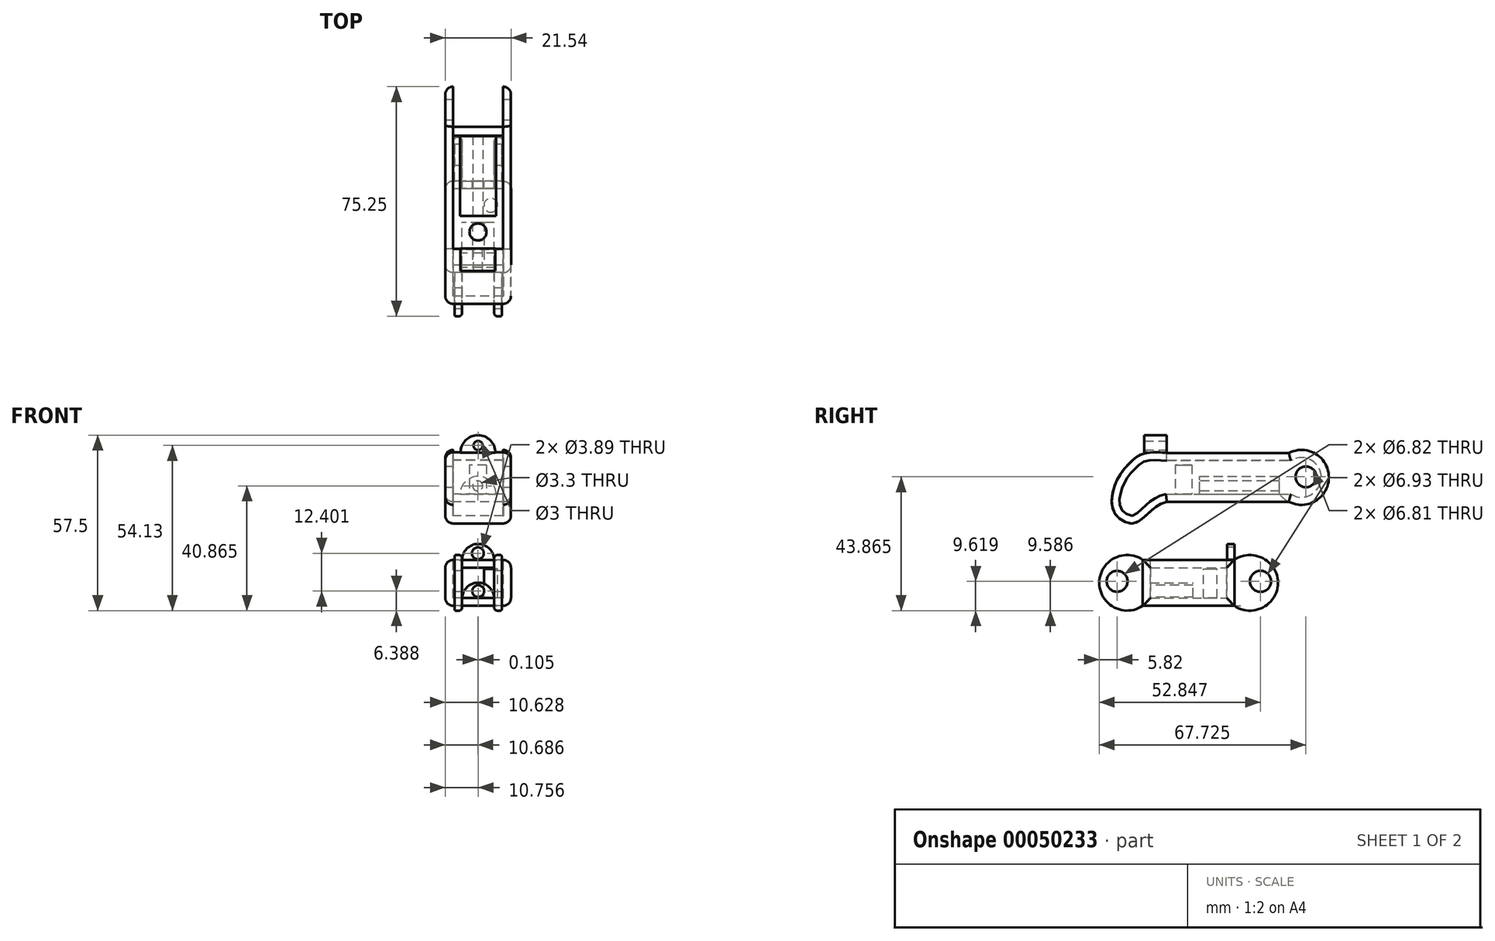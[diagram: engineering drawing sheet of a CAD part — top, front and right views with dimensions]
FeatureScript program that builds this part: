
annotation { "Feature Type Name" : "Feature", "Feature Type Description" : "" }
export const myFeature = defineFeature(function(context is Context, id is Id, definition is map)
    precondition{}
    {
        {
            var Q0;
            Q0=qCreatedBy(makeId("Right.planeOp"),FACE);
            var sketch = newSketch(context, id + "F0", { "sketchPlane" : qUnion([Q0])});
            skLineSegment(sketch, "E0.bottom", {"start": v(-17.03, 8) * mm, "end": v(22.97, 8) * mm});
            skLineSegment(sketch, "E0.top", {"start": v(-17.03, -8) * mm, "end": v(22.97, -8) * mm});
            skLineSegment(sketch, "E0.right", {"start": v(22.97, 8) * mm, "end": v(22.97, -8) * mm});
            skFitSpline(sketch, "E1", {"points": [v(-17.03, 8) * mm, v(-23.95, 8) * mm, v(-29.12, 4.72) * mm, v(-32.9, 0) * mm, v(-35.08, -8.22) * mm, v(-32.93, -13.14) * mm, v(-27.16, -14.86) * mm, v(-17.03, -8) * mm], "startDerivative": vector(-10.66, 0) * mm, "endDerivative": vector(74.6, 17.35) * mm});
            skLineSegment(sketch, "E2", {"start": v(-17.03, 8) * mm, "end": v(-17.03, -8) * mm});
            skArc(sketch, "E3", {"start": v(22.97, -8) * mm, "mid": v(36.1, 0) * mm, "end": v(22.97, 8) * mm});
            skLineSegment(sketch, "E4", {"start": v(-35.08, 39.3) * mm, "end": v(22.97, 39.3) * mm, "construction": true});
            skSolve(sketch);
        }
        {
            var Q0;
            Q0 = qSketchRegion(id + "F0", true);
            extrude(context, id + "F1", {"entities" : qUnion([Q0]), "depth" : 21.53 * mm});
        }
        {
            var Q0;
            Q0=makeQuery(id+"F1.opExtrude","CAP_EDGE",EDGE,{"disambiguationData":[OSD([sQuery(id+"F0.wireOp",EDGE,"E1")])],"isStart":false});
            var Q1;
            Q1=makeQuery(id+"F1.opExtrude","CAP_EDGE",EDGE,{"disambiguationData":[OSD([sQuery(id+"F0.wireOp",EDGE,"E0.bottom")])],"isStart":false});
            var Q2;
            Q2=makeQuery(id+"F1.opExtrude","CAP_EDGE",EDGE,{"disambiguationData":[OSD([sQuery(id+"F0.wireOp",EDGE,"E0.top")])],"isStart":false});
            var Q3;
            Q3=makeQuery(id+"F1.opExtrude","CAP_EDGE",EDGE,{"disambiguationData":[OSD([sQuery(id+"F0.wireOp",EDGE,"E0.right")])],"isStart":false});
            var Q4;
            Q4=makeQuery(id+"F1.opExtrude","CAP_EDGE",EDGE,{"disambiguationData":[OSD([sQuery(id+"F0.wireOp",EDGE,"ce066866-ab93-4ea4-af78-5b55cf1db8a8")])],"isStart":false});
            var Q5;
            Q5=makeQuery(id+"F1.opExtrude","CAP_EDGE",EDGE,{"disambiguationData":[OSD([sQuery(id+"F0.wireOp",EDGE,"E3")])],"isStart":false});
            fillet(context, id + "F2", {"entities" : qUnion([Q0, Q1, Q2, Q3, Q4, Q5]), "radius" : 2.54 * mm, "tangentPropagation" : true, "allowEdgeOverflow" : false});
        }
        {
            var Q0;
            Q0=makeQuery(id+"F1.opExtrude","CAP_EDGE",EDGE,{"disambiguationData":[OSD([sQuery(id+"F0.wireOp",EDGE,"E0.bottom")])],"isStart":true});
            var Q1;
            Q1=makeQuery(id+"F1.opExtrude","CAP_EDGE",EDGE,{"disambiguationData":[OSD([sQuery(id+"F0.wireOp",EDGE,"E1")])],"isStart":true});
            var Q2;
            Q2=makeQuery(id+"F1.opExtrude","CAP_FACE",FACE,{"disambiguationData":[OSD([sQuery(id+"F0.wireOp",EDGE,"E0.bottom"),sQuery(id+"F0.wireOp",EDGE,"E0.top"),sQuery(id+"F0.wireOp",EDGE,"E0.right"),sQuery(id+"F0.wireOp",EDGE,"E1")])],"isStart":true});
            var Q3;
            Q3=makeQuery(id+"F1.opExtrude","CAP_EDGE",EDGE,{"disambiguationData":[OSD([sQuery(id+"F0.wireOp",EDGE,"E0.top")])],"isStart":true});
            var Q4;
            Q4=makeQuery(id+"F1.opExtrude","CAP_EDGE",EDGE,{"disambiguationData":[OSD([sQuery(id+"F0.wireOp",EDGE,"E0.right")])],"isStart":true});
            fillet(context, id + "F3", {"entities" : qUnion([Q0, Q1, Q2, Q3, Q4]), "radius" : 2.54 * mm, "tangentPropagation" : true, "allowEdgeOverflow" : false});
        }
        {
            var Q0;
            Q0=makeQuery(id+"F1.opExtrude","SWEPT_FACE",FACE,{"disambiguationData":[OSD([sQuery(id+"F0.wireOp",EDGE,"E0.bottom")])]});
            var Q1;
            Q1=makeQuery(id+"F1.opExtrude","SWEPT_FACE",FACE,{"disambiguationData":[OSD([sQuery(id+"F0.wireOp",EDGE,"E3")])]});
            shell(context, id + "F4", {"entities" : qUnion([Q0, Q1]), "thickness" : 2.5 * mm});
        }
        {
            var Q0;
            Q0=qCreatedBy(makeId("Right.planeOp"),FACE);
            var sketch = newSketch(context, id + "F5", { "sketchPlane" : qUnion([Q0])});
            skCircle(sketch, "E5", {"center": v(28.57, 0.19) * mm, "radius": 3.4 * mm});
            skSolve(sketch);
        }
        {
            var Q0;
            Q0 = qSketchRegion(id + "F5", true);
            extrude(context, id + "F6", {"entities" : qUnion([Q0]), "operationType" : NewBodyOperationType.REMOVE, "oppositeDirection" : true, "depth" : 25 * mm, "hasSecondDirection" : true, "secondDirectionOppositeDirection" : false, "secondDirectionDepth" : 25 * mm});
        }
        {
            var Q0;
            Q0=qCreatedBy(makeId("Front.planeOp"),FACE);
            var sketch = newSketch(context, id + "F7", { "sketchPlane" : qUnion([Q0])});
            skLineSegment(sketch, "E6", {"start": v(2.57, -5.6) * mm, "end": v(18.95, -5.6) * mm});
            skArc(sketch, "E7", {"start": v(16.68, -5.6) * mm, "mid": v(10.76, 0.32) * mm, "end": v(4.84, -5.6) * mm});
            skSolve(sketch);
        }
        {
            var Q0;
            Q0 = qSketchRegion(id + "F7", true);
            var Q1;
            Q1=makeQuery(id+"F1.opExtrude","SWEPT_BODY",BODY,{"disambiguationData":[OSD([sQuery(id+"F0.wireOp",EDGE,"E0.bottom"),sQuery(id+"F0.wireOp",EDGE,"E0.top"),sQuery(id+"F0.wireOp",EDGE,"E1"),sQuery(id+"F0.wireOp",EDGE,"ce066866-ab93-4ea4-af78-5b55cf1db8a8")])]});
            extrude(context, id + "F8", {"entities" : qUnion([Q0]), "operationType" : NewBodyOperationType.ADD, "endBoundEntityBody" : qUnion([Q1]), "depth" : 6.26 * mm, "hasSecondDirection" : true, "secondDirectionOppositeDirection" : true, "secondDirectionDepth" : 19.94 * mm});
        }
        {
            var Q0;
            Q0=qCreatedBy(makeId("Front.planeOp"),FACE);
            var sketch = newSketch(context, id + "F9", { "sketchPlane" : qUnion([Q0])});
            skCircle(sketch, "E8", {"center": v(10.63, -2.81) * mm, "radius": 1.65 * mm});
            skSolve(sketch);
        }
        {
            var Q0;
            Q0 = qSketchRegion(id + "F9", true);
            extrude(context, id + "F10", {"entities" : qUnion([Q0]), "operationType" : NewBodyOperationType.REMOVE, "oppositeDirection" : true, "depth" : 23.72 * mm, "hasSecondDirection" : true, "secondDirectionOppositeDirection" : false, "secondDirectionDepth" : 7.27 * mm});
        }
        {
            var Q0;
            Q0=qCreatedBy(makeId("Top.planeOp"),FACE);
            var sketch = newSketch(context, id + "F11", { "sketchPlane" : qUnion([Q0])});
            skCircle(sketch, "E9", {"center": v(10.72, -11.53) * mm, "radius": 2.78 * mm});
            skSolve(sketch);
        }
        {
            var Q0;
            Q0=makeQuery(id+"F11.imprint","IMPRINT",FACE,{"disambiguationData":[TD([[makeQuery(id+"F11.imprint","IMPRINT",EDGE,{"derivedFrom":sQuery(id+"F11.wireOp",EDGE,"E9")}),1.0]])]});
            extrude(context, id + "F12", {"entities" : qUnion([Q0]), "operationType" : NewBodyOperationType.ADD, "depth" : 4.07 * mm, "hasSecondDirection" : true, "secondDirectionOppositeDirection" : true, "secondDirectionDepth" : 5.54 * mm});
        }
        {
            var Q0;
            Q0=qCreatedBy(makeId("Front.planeOp"),FACE);
            var sketch = newSketch(context, id + "F13", { "sketchPlane" : qUnion([Q0])});
            skLineSegment(sketch, "E10", {"start": v(1.36, 8.11) * mm, "end": v(20.04, 8.11) * mm});
            skPoint(sketch, "E11", {"position": v(10.7, 8.11) * mm});
            skArc(sketch, "E12", {"start": v(16.4, 8.11) * mm, "mid": v(10.7, 13.82) * mm, "end": v(5, 8.11) * mm});
            skSolve(sketch);
        }
        {
            var Q0;
            {var subQ0=sQuery(id+"F13.wireOp",EDGE,"E12");Q0=makeQuery(id+"F13.imprint","IMPRINT",FACE,{"disambiguationData":[TD([[makeQuery(id+"F13.imprint","IMPRINT",EDGE,{"derivedFrom":subQ0}),1.0]])]});}
            extrude(context, id + "F14", {"entities" : qUnion([Q0]), "operationType" : NewBodyOperationType.ADD, "depth" : 24.37 * mm, "hasSecondDirection" : true, "secondDirectionOppositeDirection" : false, "secondDirectionDepth" : 17 * mm});
        }
        {
            var Q0;
            Q0=qCreatedBy(makeId("Front.planeOp"),FACE);
            var sketch = newSketch(context, id + "F15", { "sketchPlane" : qUnion([Q0])});
            skCircle(sketch, "E13", {"center": v(10.76, 10.45) * mm, "radius": 1.5 * mm});
            skSolve(sketch);
        }
        {
            var Q0;
            Q0 = qSketchRegion(id + "F15", true);
            extrude(context, id + "F16", {"entities" : qUnion([Q0]), "operationType" : NewBodyOperationType.REMOVE, "depth" : 25.52 * mm, "hasSecondDirection" : true, "secondDirectionOppositeDirection" : false, "secondDirectionDepth" : 12.6 * mm});
        }
        {
            var Q0;
            Q0=qCreatedBy(makeId("Right.planeOp"),FACE);
            var sketch = newSketch(context, id + "F17", { "sketchPlane" : qUnion([Q0])});
            skLineSegment(sketch, "E14.bottom", {"start": v(-24.87, -27.08) * mm, "end": v(5.13, -27.08) * mm});
            skLineSegment(sketch, "E14.top", {"start": v(-24.87, -42.08) * mm, "end": v(5.13, -42.08) * mm});
            skLineSegment(sketch, "E14.left", {"start": v(-24.87, -27.08) * mm, "end": v(-24.87, -42.08) * mm});
            skLineSegment(sketch, "E14.right", {"start": v(5.13, -27.08) * mm, "end": v(5.13, -42.08) * mm});
            skArc(sketch, "E15", {"start": v(22.8, -7.92) * mm, "mid": v(36.26, 0.1) * mm, "end": v(22.8, 8.1) * mm});
            skSolve(sketch);
        }
        {
            var Q0;
            Q0 = qSketchRegion(id + "F17", true);
            extrude(context, id + "F18", {"entities" : qUnion([Q0]), "depth" : 21.54 * mm});
        }
        {
            var Q0;
            Q0=qCreatedBy(makeId("Right.planeOp"),FACE);
            var sketch = newSketch(context, id + "F19", { "sketchPlane" : qUnion([Q0])});
            skArc(sketch, "E16", {"start": v(22.81, -8) * mm, "mid": v(36.02, 0.21) * mm, "end": v(22.66, 8.17) * mm});
            skArc(sketch, "E17", {"start": v(5.06, -42.03) * mm, "mid": v(19.39, -34.6) * mm, "end": v(5.1, -27.1) * mm});
            skArc(sketch, "E18", {"start": v(-24.84, -27.1) * mm, "mid": v(-39.15, -34.58) * mm, "end": v(-24.84, -42.03) * mm});
            skLineSegment(sketch, "E19", {"start": v(-24.84, -27.1) * mm, "end": v(-24.84, -42.03) * mm});
            skLineSegment(sketch, "E20", {"start": v(5.1, -27.1) * mm, "end": v(5.06, -42.03) * mm});
            skSolve(sketch);
        }
        {
            var Q0;
            Q0 = qSketchRegion(id + "F19", true);
            extrude(context, id + "F20", {"entities" : qUnion([Q0]), "operationType" : NewBodyOperationType.ADD, "depth" : 18.54 * mm, "hasSecondDirection" : true, "secondDirectionOppositeDirection" : false, "secondDirectionDepth" : 3 * mm});
        }
        {
            var Q0;
            Q0=makeQuery(id+"F18.opExtrude","CAP_EDGE",EDGE,{"disambiguationData":[OSD([sQuery(id+"F17.wireOp",EDGE,"E14.bottom")])],"isStart":false});
            var Q1;
            Q1=makeQuery(id+"F18.opExtrude","CAP_EDGE",EDGE,{"disambiguationData":[OSD([sQuery(id+"F17.wireOp",EDGE,"E14.top")])],"isStart":false});
            var Q2;
            Q2=makeQuery(id+"F18.opExtrude","CAP_EDGE",EDGE,{"disambiguationData":[OSD([sQuery(id+"F17.wireOp",EDGE,"E14.bottom")])],"isStart":true});
            var Q3;
            Q3=makeQuery(id+"F18.opExtrude","CAP_EDGE",EDGE,{"disambiguationData":[OSD([sQuery(id+"F17.wireOp",EDGE,"E14.top")])],"isStart":true});
            var Q4;
            Q4=makeQuery(id+"F18.opExtrude","CAP_EDGE",EDGE,{"disambiguationData":[OSD([sQuery(id+"F17.wireOp",EDGE,"E14.right")])],"isStart":true});
            var Q5;
            Q5=makeQuery(id+"F18.opExtrude","CAP_EDGE",EDGE,{"disambiguationData":[OSD([sQuery(id+"F17.wireOp",EDGE,"E14.left")])],"isStart":true});
            var Q6;
            Q6=makeQuery(id+"F18.opExtrude","CAP_EDGE",EDGE,{"disambiguationData":[OSD([sQuery(id+"F17.wireOp",EDGE,"E14.right")])],"isStart":false});
            var Q7;
            Q7=makeQuery(id+"F18.opExtrude","CAP_EDGE",EDGE,{"disambiguationData":[OSD([sQuery(id+"F17.wireOp",EDGE,"E14.left")])],"isStart":false});
            fillet(context, id + "F21", {"entities" : qUnion([Q0, Q1, Q2, Q3, Q4, Q5, Q6, Q7]), "radius" : 2.54 * mm, "allowEdgeOverflow" : false});
        }
        {
            var Q0;
            Q0=makeQuery(id+"F18.opExtrude","SWEPT_FACE",FACE,{"disambiguationData":[OSD([sQuery(id+"F17.wireOp",EDGE,"E14.bottom")])]});
            var Q1;
            Q1=makeQuery(id+"F20.opExtrude","SWEPT_FACE",FACE,{"disambiguationData":[OSD([sQuery(id+"F19.wireOp",EDGE,"E18")])]});
            var Q2;
            Q2=makeQuery(id+"F20.opExtrude","SWEPT_FACE",FACE,{"disambiguationData":[OSD([sQuery(id+"F19.wireOp",EDGE,"E17")])]});
            shell(context, id + "F22", {"entities" : qUnion([Q0, Q1, Q2]), "thickness" : 2.5 * mm});
        }
        {
            var Q0;
            Q0=qCreatedBy(makeId("Right.planeOp"),FACE);
            var sketch = newSketch(context, id + "F23", { "sketchPlane" : qUnion([Q0])});
            skCircle(sketch, "E21", {"center": v(13.7, -34.1) * mm, "radius": 3.47 * mm});
            skCircle(sketch, "E22", {"center": v(-33.33, -34.06) * mm, "radius": 3.41 * mm});
            skSolve(sketch);
        }
        {
            var Q0;
            {var subQ0=sQuery(id+"F19.wireOp",EDGE,"E18");Q0=makeQuery(id+"F22.opShell","OFFSET_EDGE",EDGE,{"disambiguationData":[OSD([subQ0]),TDD([makeQuery(id+"F20.opExtrude","CAP_EDGE",EDGE,{"disambiguationData":[OSD([subQ0])],"isStart":false})]),OD(2.0)]});}
            var Q1;
            {var subQ0=sQuery(id+"F19.wireOp",EDGE,"E18");Q1=makeQuery(id+"F22.opShell","OFFSET_EDGE",EDGE,{"disambiguationData":[OSD([subQ0]),TDD([makeQuery(id+"F20.opExtrude","CAP_EDGE",EDGE,{"disambiguationData":[OSD([subQ0])],"isStart":true})]),OD(2.0)]});}
            var Q2;
            {var subQ0=sQuery(id+"F19.wireOp",EDGE,"E17");Q2=makeQuery(id+"F22.opShell","OFFSET_EDGE",EDGE,{"disambiguationData":[OSD([subQ0]),TDD([makeQuery(id+"F20.opExtrude","CAP_EDGE",EDGE,{"disambiguationData":[OSD([subQ0])],"isStart":true})]),OD(2.0)]});}
            var Q3;
            {var subQ0=sQuery(id+"F19.wireOp",EDGE,"E17");Q3=makeQuery(id+"F22.opShell","OFFSET_EDGE",EDGE,{"disambiguationData":[OSD([subQ0]),TDD([makeQuery(id+"F20.opExtrude","CAP_EDGE",EDGE,{"disambiguationData":[OSD([subQ0])],"isStart":false})]),OD(0.0)]});}
            fillet(context, id + "F24", {"entities" : qUnion([Q0, Q1, Q2, Q3]), "radius" : 1 * mm, "tangentPropagation" : true, "allowEdgeOverflow" : false});
        }
        {
            var Q0;
            Q0=qCreatedBy(makeId("Front.planeOp"),FACE);
            var sketch = newSketch(context, id + "F25", { "sketchPlane" : qUnion([Q0])});
            skLineSegment(sketch, "E23", {"start": v(16, -39.48) * mm, "end": v(5.52, -39.48) * mm});
            skPoint(sketch, "E24", {"position": v(10.76, -39.48) * mm});
            skArc(sketch, "E25", {"start": v(16, -39.48) * mm, "mid": v(10.76, -34.53) * mm, "end": v(5.52, -39.48) * mm});
            skSolve(sketch);
        }
        {
            var Q0;
            Q0 = qSketchRegion(id + "F25", true);
            extrude(context, id + "F26", {"entities" : qUnion([Q0]), "operationType" : NewBodyOperationType.ADD, "depth" : 22.42 * mm, "hasSecondDirection" : true, "secondDirectionOppositeDirection" : false, "secondDirectionDepth" : 8.4 * mm});
        }
        {
            var Q0;
            Q0=qCreatedBy(makeId("Front.planeOp"),FACE);
            var sketch = newSketch(context, id + "F27", { "sketchPlane" : qUnion([Q0])});
            skArc(sketch, "E26", {"start": v(16.03, -27.1) * mm, "mid": v(10.77, -21.83) * mm, "end": v(5.5, -27.09) * mm});
            skLineSegment(sketch, "E27", {"start": v(5.5, -27.09) * mm, "end": v(16.03, -27.1) * mm});
            skSolve(sketch);
        }
        {
            var Q0;
            Q0=makeQuery(id+"F27.imprint","IMPRINT",FACE,{"disambiguationData":[TD([[makeQuery(id+"F27.imprint","IMPRINT",EDGE,{"derivedFrom":sQuery(id+"F27.wireOp",EDGE,"E26")}),1.0]])]});
            extrude(context, id + "F28", {"entities" : qUnion([Q0]), "operationType" : NewBodyOperationType.ADD, "oppositeDirection" : true, "depth" : 5.16 * mm, "hasSecondDirection" : true, "secondDirectionOppositeDirection" : true, "secondDirectionDepth" : 2.77 * mm});
        }
        {
            var Q0;
            Q0=makeQuery(id+"F20.opExtrude","CAP_EDGE",EDGE,{"disambiguationData":[OSD([sQuery(id+"F19.wireOp",EDGE,"E18")])],"isStart":true});
            var Q1;
            Q1=makeQuery(id+"F20.opExtrude","CAP_EDGE",EDGE,{"disambiguationData":[OSD([sQuery(id+"F19.wireOp",EDGE,"E18")])],"isStart":false});
            var Q2;
            Q2=makeQuery(id+"F20.opExtrude","CAP_EDGE",EDGE,{"disambiguationData":[OSD([sQuery(id+"F19.wireOp",EDGE,"E17")])],"isStart":true});
            var Q3;
            Q3=makeQuery(id+"F20.opExtrude","CAP_EDGE",EDGE,{"disambiguationData":[OSD([sQuery(id+"F19.wireOp",EDGE,"E17")])],"isStart":false});
            fillet(context, id + "F29", {"entities" : qUnion([Q0, Q1, Q2, Q3]), "radius" : .5 * mm, "tangentPropagation" : true, "allowEdgeOverflow" : false});
        }
        {
            var Q0;
            Q0 = qSketchRegion(id + "F23", true);
            extrude(context, id + "F30", {"entities" : qUnion([Q0]), "operationType" : NewBodyOperationType.REMOVE, "depth" : 25 * mm});
        }
        {
            var Q0;
            Q0=qCreatedBy(makeId("Front.planeOp"),FACE);
            var sketch = newSketch(context, id + "F31", { "sketchPlane" : qUnion([Q0])});
            skCircle(sketch, "E28", {"center": v(10.8, -37.3) * mm, "radius": 1.94 * mm});
            skCircle(sketch, "E29", {"center": v(10.69, -24.9) * mm, "radius": 1.94 * mm});
            skSolve(sketch);
        }
        {
            var Q0;
            Q0 = qSketchRegion(id + "F31", true);
            var Q1;
            Q1=makeQuery(id+"F31.imprint","IMPRINT",FACE,{"disambiguationData":[TD([[makeQuery(id+"F31.imprint","IMPRINT",EDGE,{"derivedFrom":sQuery(id+"F31.wireOp",EDGE,"E28")}),1.0]])]});
            extrude(context, id + "F32", {"entities" : qUnion([Q0, Q1]), "operationType" : NewBodyOperationType.REMOVE, "oppositeDirection" : true, "depth" : 32.5 * mm, "hasSecondDirection" : true, "secondDirectionOppositeDirection" : false, "secondDirectionDepth" : 46.88 * mm});
        }
        {
            var Q0;
            Q0=qCreatedBy(makeId("Top.planeOp"),FACE);
            var sketch = newSketch(context, id + "F33", { "sketchPlane" : qUnion([Q0])});
            skCircle(sketch, "E30", {"center": v(14.92, -2.78) * mm, "radius": 2.28 * mm});
            skSolve(sketch);
        }
        {
            var Q0;
            Q0 = qSketchRegion(id + "F33", true);
            extrude(context, id + "F34", {"entities" : qUnion([Q0]), "operationType" : NewBodyOperationType.ADD, "oppositeDirection" : true, "depth" : 40.02 * mm, "hasSecondDirection" : true, "secondDirectionOppositeDirection" : true, "secondDirectionDepth" : 29.95 * mm});
        }
    });
